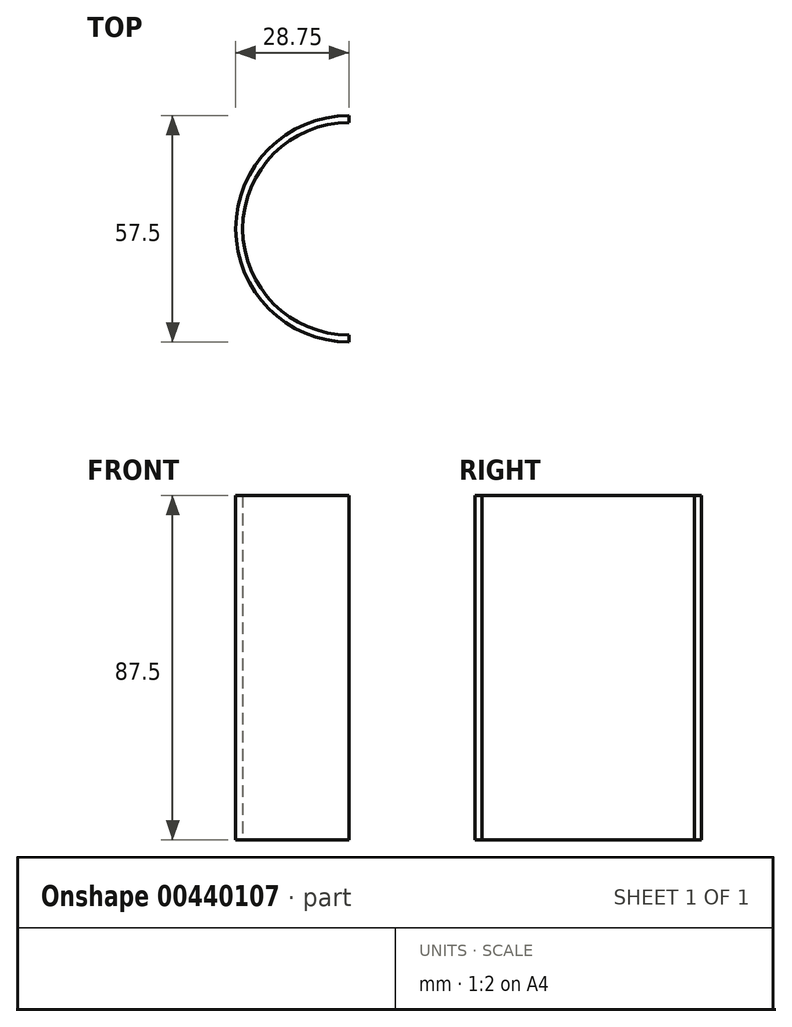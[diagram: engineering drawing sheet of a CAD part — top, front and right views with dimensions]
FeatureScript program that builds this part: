
annotation { "Feature Type Name" : "Feature", "Feature Type Description" : "" }
export const myFeature = defineFeature(function(context is Context, id is Id, definition is map)
    precondition{}
    {
        {
            var Q0;
            Q0=qCreatedBy(makeId("Top.planeOp"),FACE);
            var sketch = newSketch(context, id + "F0", { "sketchPlane" : qUnion([Q0])});
            skCircle(sketch, "E0", {"center": v(0, 0) * mm, "radius": 28.75 * mm});
            skCircle(sketch, "E1", {"center": v(0, 0) * mm, "radius": 27 * mm});
            skCircle(sketch, "E2", {"center": v(0, 0) * mm, "radius": 25 * mm});
            skLineSegment(sketch, "E3", {"start": v(0, 28.75) * mm, "end": v(0, -28.75) * mm});
            skLineSegment(sketch, "E4", {"start": v(0, 0) * mm, "end": v(28.75, 0) * mm, "construction": true});
            skSolve(sketch);
        }
        {
            var Q0;
            {var subQ0=sQuery(id+"F0.wireOp",EDGE,"E3");var subQ1=sQuery(id+"F0.wireOp",EDGE,"E0");var subQ2=makeQuery(id+"F0.imprint","INTERSECT",VERTEX,{"disambiguationData":[OD(0.0)],"derivedFrom":[subQ1,subQ0]});Q0=makeQuery(id+"F0.imprint","IMPRINT",FACE,{"disambiguationData":[TD([[makeQuery(id+"F0.imprint","IMPRINT",EDGE,{"disambiguationData":[TD([[subQ2,1.0]])],"derivedFrom":subQ1}),1.0]])]});}
            extrude(context, id + "F1", {"entities" : qUnion([Q0]), "depth" : (175 / 2) * mm, "offsetDistance" : 25 * mm});
        }
        {
            var Q0;
            Q0=qCreatedBy(makeId("Front.planeOp"),FACE);
            var sketch = newSketch(context, id + "F2", { "sketchPlane" : qUnion([Q0])});
            skLineSegment(sketch, "E5", {"start": v(0, 0) * mm, "end": v(0, 43.75) * mm, "construction": true});
            skLineSegment(sketch, "E6", {"start": v(0, 43.75) * mm, "end": v(0, 87.5) * mm, "construction": true});
            skLineSegment(sketch, "E7", {"start": v(0, 43.75) * mm, "end": v(28.75, 43.75) * mm, "construction": true});
            skLineSegment(sketch, "E8", {"start": v(0, 87.5) * mm, "end": v(28.75, 87.5) * mm, "construction": true});
            skLineSegment(sketch, "E9", {"start": v(0, 65.62) * mm, "end": v(28.75, 65.62) * mm, "construction": true});
            skLineSegment(sketch, "E10", {"start": v(0, 21.88) * mm, "end": v(28.75, 21.88) * mm, "construction": true});
            skLineSegment(sketch, "E11.MirrorCS", {"start": v(0, -43.75) * mm, "end": v(28.75, -43.75) * mm, "construction": true});
            skLineSegment(sketch, "E12.MirrorCS", {"start": v(0, -65.62) * mm, "end": v(28.75, -65.62) * mm, "construction": true});
            skLineSegment(sketch, "E13.MirrorCS", {"start": v(0, -21.88) * mm, "end": v(28.75, -21.88) * mm, "construction": true});
            skLineSegment(sketch, "E14.MirrorCS", {"start": v(0, 0) * mm, "end": v(0, -43.75) * mm, "construction": true});
            skLineSegment(sketch, "E15.MirrorCS", {"start": v(0, -43.75) * mm, "end": v(0, -87.5) * mm, "construction": true});
            skLineSegment(sketch, "E16.MirrorCS", {"start": v(0, -87.5) * mm, "end": v(28.75, -87.5) * mm, "construction": true});
            skSolve(sketch);
        }
        {
            var Q0;
            Q0=qCreatedBy(makeId("Right.planeOp"),FACE);
            var sketch = newSketch(context, id + "F3", { "sketchPlane" : qUnion([Q0])});
            skLineSegment(sketch, "E17.0", {"start": v(0, 0) * mm, "end": v(0, 43.75) * mm, "construction": true});
            skLineSegment(sketch, "E18.0", {"start": v(0, 43.75) * mm, "end": v(0, 87.5) * mm, "construction": true});
            skLineSegment(sketch, "E19.0", {"start": v(0, 0) * mm, "end": v(0, -43.75) * mm, "construction": true});
            skLineSegment(sketch, "E20.0", {"start": v(0, -43.75) * mm, "end": v(0, -87.5) * mm, "construction": true});
            skCircle(sketch, "E21", {"center": v(0, 43.75) * mm, "radius": 1.5 * mm});
            skCircle(sketch, "E22", {"center": v(0, -43.75) * mm, "radius": 1.5 * mm});
            skCircle(sketch, "E23", {"center": v(0, 65.62) * mm, "radius": 1.5 * mm});
            skCircle(sketch, "E24", {"center": v(0, 21.88) * mm, "radius": 1.5 * mm});
            skSolve(sketch);
        }
        {
            var Q0;
            Q0=makeQuery(id+"F3.imprint","IMPRINT",FACE,{"disambiguationData":[TD([[makeQuery(id+"F3.imprint","IMPRINT",EDGE,{"derivedFrom":sQuery(id+"F3.wireOp",EDGE,"E23")}),1.0]])]});
            var Q1;
            Q1=makeQuery(id+"F3.imprint","IMPRINT",FACE,{"disambiguationData":[TD([[makeQuery(id+"F3.imprint","IMPRINT",EDGE,{"derivedFrom":sQuery(id+"F3.wireOp",EDGE,"E24")}),1.0]])]});
            var Q2;
            Q2=sQuery(id+"F3.wireOp",EDGE,"E21");
            var Q3;
            Q3=sQuery(id+"F3.wireOp",EDGE,"E22");
            extrude(context, id + "F4", {"entities" : qUnion([Q0, Q1]), "operationType" : NewBodyOperationType.REMOVE, "surfaceEntities" : qUnion([Q2, Q3]), "endBound" : BoundingType.THROUGH_ALL, "depth" : 25 * mm, "offsetDistance" : 25 * mm});
        }
    });
